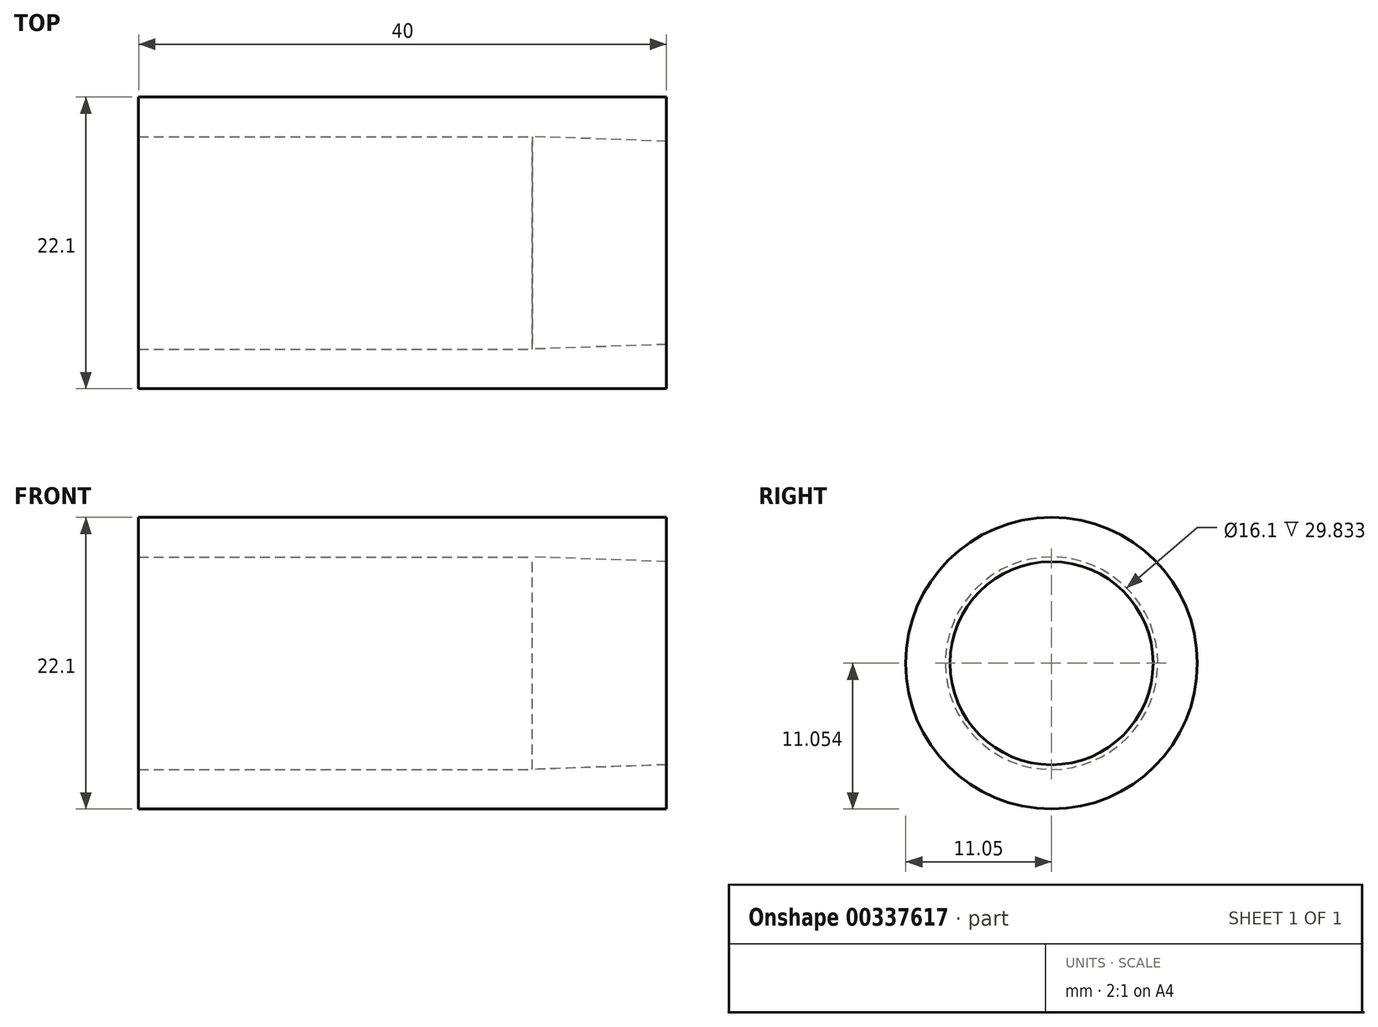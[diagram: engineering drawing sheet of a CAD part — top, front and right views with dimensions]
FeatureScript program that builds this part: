
annotation { "Feature Type Name" : "Feature", "Feature Type Description" : "" }
export const myFeature = defineFeature(function(context is Context, id is Id, definition is map)
    precondition{}
    {
        {
            var Q0;
            Q0=qCreatedBy(makeId("Front.planeOp"),FACE);
            var sketch = newSketch(context, id + "F0", { "sketchPlane" : qUnion([Q0])});
            skLineSegment(sketch, "E0", {"start": v(-13.18, 0.34) * mm, "end": v(-23.01, 0.34) * mm});
            skLineSegment(sketch, "E1", {"start": v(16.99, 3.34) * mm, "end": v(-23.01, 3.34) * mm});
            skLineSegment(sketch, "E2", {"start": v(-23.01, 3.34) * mm, "end": v(-23.01, 0.34) * mm});
            skLineSegment(sketch, "E3", {"start": v(34.85, -7.7) * mm, "end": v(1.99, -7.7) * mm, "construction": true});
            skLineSegment(sketch, "E4", {"start": v(6.82, 0.34) * mm, "end": v(-13.18, 0.34) * mm});
            skLineSegment(sketch, "E5", {"start": v(16.99, 3.34) * mm, "end": v(16.99, -0.01) * mm});
            skLineSegment(sketch, "E6", {"start": v(16.99, -0.01) * mm, "end": v(6.82, 0.34) * mm});
            skSolve(sketch);
        }
        {
            var Q0;
            Q0=makeQuery(id+"F0.imprint","IMPRINT",FACE,{"disambiguationData":[TD([[makeQuery(id+"F0.imprint","IMPRINT",EDGE,{"derivedFrom":sQuery(id+"F0.wireOp",EDGE,"E0")}),-1.0]])]});
            var Q1;
            Q1=sQuery(id+"F0.wireOp",EDGE,"E3");
            revolve(context, id + "F1", {"entities" : qUnion([Q0]), "axis" : qUnion([Q1]), "revolveType" : RevolveType.FULL});
        }
    });
